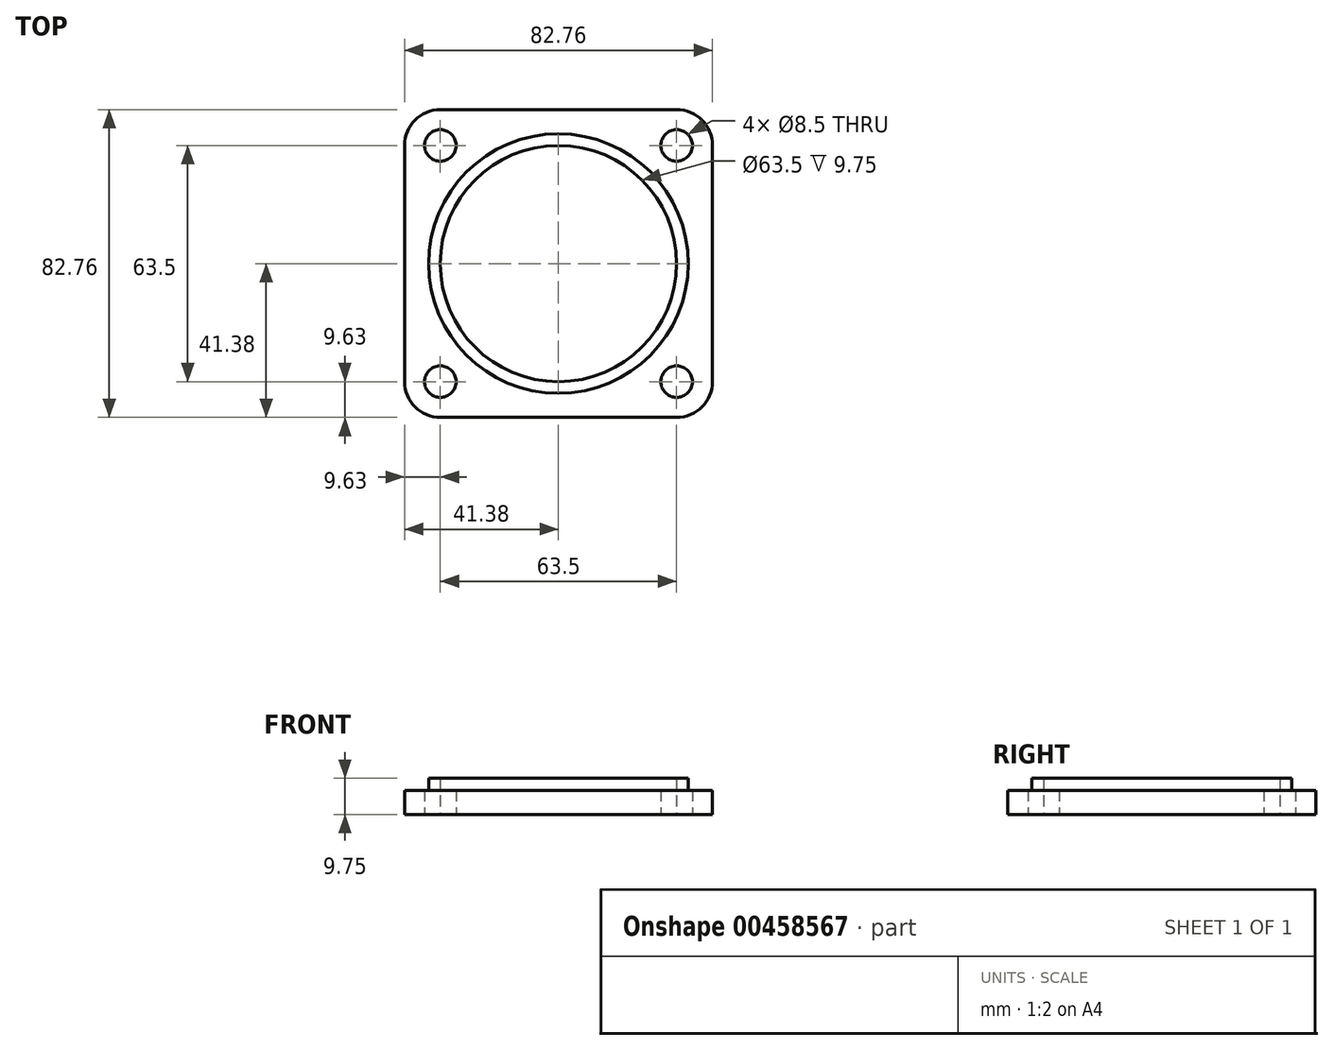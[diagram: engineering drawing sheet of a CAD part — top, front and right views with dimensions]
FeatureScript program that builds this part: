
annotation { "Feature Type Name" : "Feature", "Feature Type Description" : "" }
export const myFeature = defineFeature(function(context is Context, id is Id, definition is map)
    precondition{}
    {
        {
            var Q0;
            Q0=qCreatedBy(makeId("Top.planeOp"),FACE);
            var sketch = newSketch(context, id + "F0", { "sketchPlane" : qUnion([Q0])});
            skLineSegment(sketch, "E0.bottom", {"start": v(-41.38, 41.38) * mm, "end": v(41.38, 41.38) * mm});
            skLineSegment(sketch, "E0.top", {"start": v(-41.38, -41.37) * mm, "end": v(41.38, -41.37) * mm});
            skLineSegment(sketch, "E0.left", {"start": v(-41.38, 41.38) * mm, "end": v(-41.38, -41.38) * mm});
            skLineSegment(sketch, "E0.right", {"start": v(41.38, 41.38) * mm, "end": v(41.38, -41.38) * mm});
            skCircle(sketch, "E1", {"center": v(0, 0) * mm, "radius": 31.75 * mm});
            skCircle(sketch, "E2", {"center": v(31.75, 31.75) * mm, "radius": 4.25 * mm});
            skCircle(sketch, "E3.MirrorC", {"center": v(-31.75, 31.75) * mm, "radius": 4.25 * mm});
            skCircle(sketch, "E4.MirrorC", {"center": v(-31.75, -31.75) * mm, "radius": 4.25 * mm});
            skCircle(sketch, "E5.MirrorC", {"center": v(31.75, -31.75) * mm, "radius": 4.25 * mm});
            skSolve(sketch);
        }
        {
            var Q0;
            Q0=makeQuery(id+"F0.imprint","IMPRINT",FACE,{"disambiguationData":[TD([[makeQuery(id+"F0.imprint","IMPRINT",EDGE,{"derivedFrom":sQuery(id+"F0.wireOp",EDGE,"E0.bottom")}),-1.0]])]});
            extrude(context, id + "F1", {"entities" : qUnion([Q0]), "depth" : 6.5 * mm});
        }
        {
            var Q0;
            Q0=makeQuery(id+"F1.opExtrude","SWEPT_EDGE",EDGE,{"disambiguationData":[OSD([sQuery(id+"F0.wireOp",EDGE,"E0.top"),sQuery(id+"F0.wireOp",EDGE,"E0.left")])]});
            var Q1;
            Q1=makeQuery(id+"F1.opExtrude","SWEPT_EDGE",EDGE,{"disambiguationData":[OSD([sQuery(id+"F0.wireOp",EDGE,"E0.bottom"),sQuery(id+"F0.wireOp",EDGE,"E0.left")])]});
            var Q2;
            Q2=makeQuery(id+"F1.opExtrude","SWEPT_EDGE",EDGE,{"disambiguationData":[OSD([sQuery(id+"F0.wireOp",EDGE,"E0.bottom"),sQuery(id+"F0.wireOp",EDGE,"E0.right")])]});
            var Q3;
            Q3=makeQuery(id+"F1.opExtrude","SWEPT_EDGE",EDGE,{"disambiguationData":[OSD([sQuery(id+"F0.wireOp",EDGE,"E0.top"),sQuery(id+"F0.wireOp",EDGE,"E0.right")])]});
            fillet(context, id + "F2", {"entities" : qUnion([Q0, Q1, Q2, Q3]), "radius" : 9.62 * mm, "tangentPropagation" : true, "allowEdgeOverflow" : false});
        }
        {
            var Q0;
            Q0=makeQuery(id+"F1.opExtrude","CAP_FACE",FACE,{"disambiguationData":[OSD([sQuery(id+"F0.wireOp",EDGE,"E0.bottom"),sQuery(id+"F0.wireOp",EDGE,"E0.top"),sQuery(id+"F0.wireOp",EDGE,"E0.left"),sQuery(id+"F0.wireOp",EDGE,"E0.right"),sQuery(id+"F0.wireOp",EDGE,"E1"),sQuery(id+"F0.wireOp",EDGE,"E2"),sQuery(id+"F0.wireOp",EDGE,"E3.MirrorC"),sQuery(id+"F0.wireOp",EDGE,"E4.MirrorC"),sQuery(id+"F0.wireOp",EDGE,"E5.MirrorC")])],"isStart":false});
            var sketch = newSketch(context, id + "F3", { "sketchPlane" : qUnion([Q0])});
            skCircle(sketch, "E6", {"center": v(0, 0) * mm, "radius": 34.88 * mm});
            skCircle(sketch, "E7", {"center": v(0, 0) * mm, "radius": 31.75 * mm});
            skSolve(sketch);
        }
        {
            var Q0;
            Q0=makeQuery(id+"F3.imprint","IMPRINT",FACE,{"disambiguationData":[TD([[makeQuery(id+"F3.imprint","IMPRINT",EDGE,{"derivedFrom":sQuery(id+"F3.wireOp",EDGE,"E6")}),1.0]])]});
            extrude(context, id + "F4", {"entities" : qUnion([Q0]), "operationType" : NewBodyOperationType.ADD, "depth" : 3.25 * mm});
        }
    });
